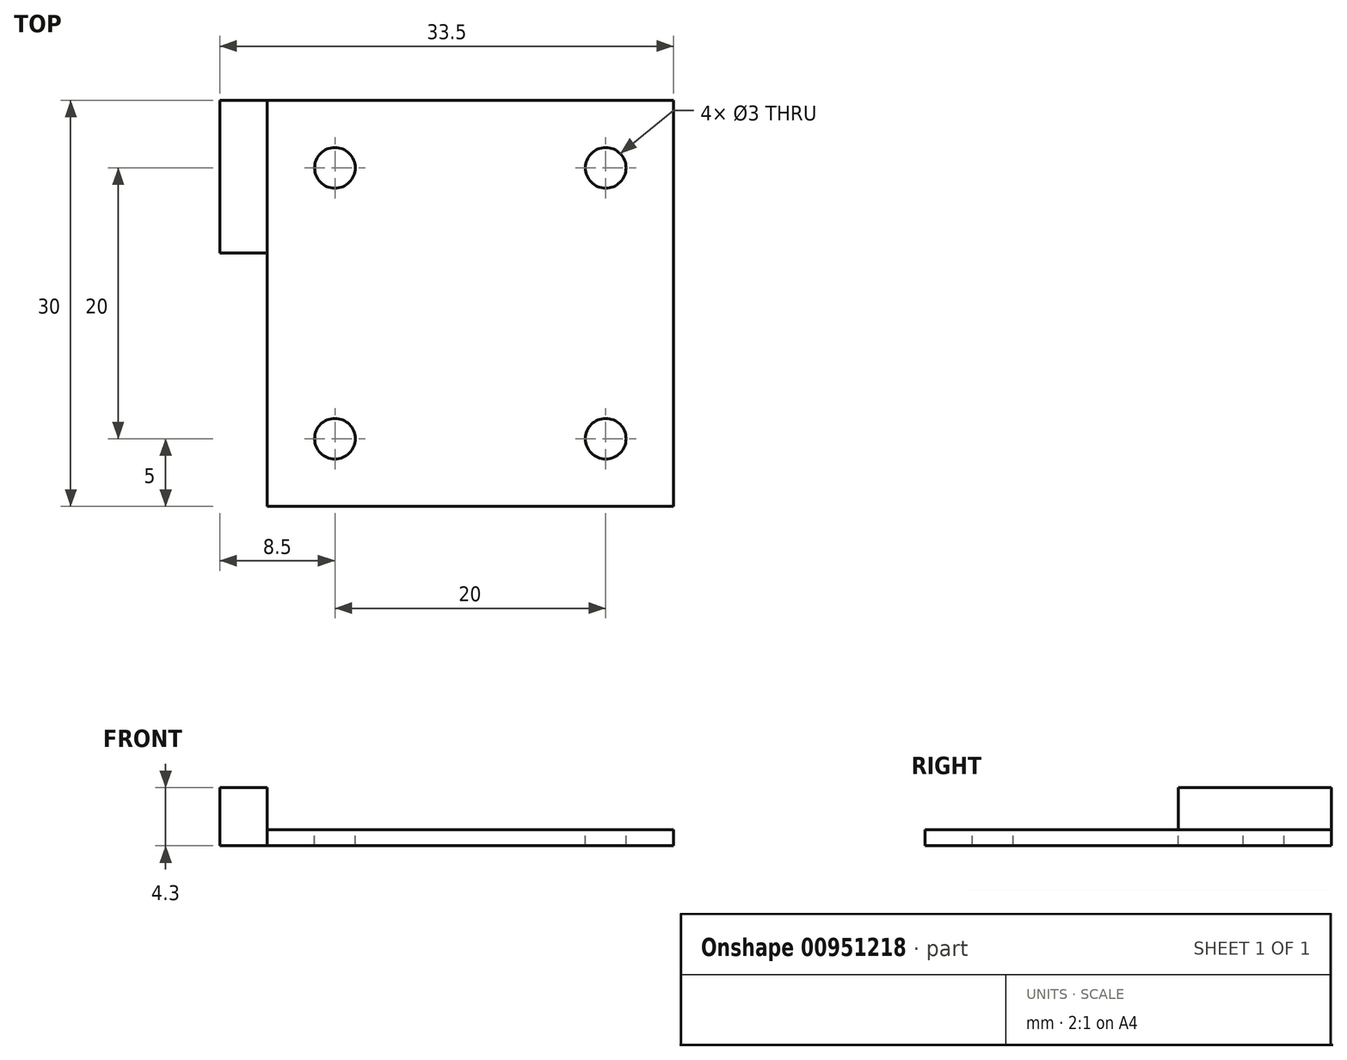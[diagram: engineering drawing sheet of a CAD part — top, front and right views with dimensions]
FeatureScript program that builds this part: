
annotation { "Feature Type Name" : "Feature", "Feature Type Description" : "" }
export const myFeature = defineFeature(function(context is Context, id is Id, definition is map)
    precondition{}
    {
        {
            var Q0;
            Q0=qCreatedBy(makeId("Top.planeOp"),FACE);
            var sketch = newSketch(context, id + "F0", { "sketchPlane" : qUnion([Q0])});
            skLineSegment(sketch, "E0.bottom", {"start": v(-15, 15) * mm, "end": v(15, 15) * mm});
            skLineSegment(sketch, "E0.top", {"start": v(-15, -15) * mm, "end": v(15, -15) * mm});
            skLineSegment(sketch, "E0.left", {"start": v(-15, 15) * mm, "end": v(-15, -15) * mm});
            skLineSegment(sketch, "E0.right", {"start": v(15, 15) * mm, "end": v(15, -15) * mm});
            skPoint(sketch, "E0.middle", {"position": v(0, 0) * mm});
            skLineSegment(sketch, "E1.bottom", {"start": v(-15, 15) * mm, "end": v(-18.5, 15) * mm});
            skLineSegment(sketch, "E1.top", {"start": v(-15, 3.7) * mm, "end": v(-18.5, 3.7) * mm});
            skLineSegment(sketch, "E1.left", {"start": v(-15, 15) * mm, "end": v(-15, 3.7) * mm});
            skLineSegment(sketch, "E1.right", {"start": v(-18.5, 15) * mm, "end": v(-18.5, 3.7) * mm});
            skCircle(sketch, "E2", {"center": v(10, 10) * mm, "radius": 1.5 * mm});
            skCircle(sketch, "E3", {"center": v(10, -10) * mm, "radius": 1.5 * mm});
            skCircle(sketch, "E4", {"center": v(-10, 10) * mm, "radius": 1.5 * mm});
            skCircle(sketch, "E5", {"center": v(-10, -10) * mm, "radius": 1.5 * mm});
            skSolve(sketch);
        }
        {
            var Q0;
            Q0=makeQuery(id+"F0.imprint","IMPRINT",FACE,{"disambiguationData":[TD([[makeQuery(id+"F0.imprint","IMPRINT",EDGE,{"derivedFrom":sQuery(id+"F0.wireOp",EDGE,"E1.bottom")}),1.0]])]});
            var Q1;
            Q1=makeQuery(id+"F0.imprint","IMPRINT",FACE,{"disambiguationData":[TD([[makeQuery(id+"F0.imprint","IMPRINT",EDGE,{"derivedFrom":sQuery(id+"F0.wireOp",EDGE,"E0.bottom")}),-1.0]])]});
            extrude(context, id + "F1", {"entities" : qUnion([Q0, Q1]), "oppositeDirection" : true, "depth" : 1.2 * mm, "offsetDistance" : 25 * mm});
        }
        {
            var Q0;
            Q0=makeQuery(id+"F0.imprint","IMPRINT",FACE,{"disambiguationData":[TD([[makeQuery(id+"F0.imprint","IMPRINT",EDGE,{"derivedFrom":sQuery(id+"F0.wireOp",EDGE,"E1.bottom")}),1.0]])]});
            extrude(context, id + "F2", {"entities" : qUnion([Q0]), "operationType" : NewBodyOperationType.ADD, "depth" : 3.1 * mm, "offsetDistance" : 25 * mm});
        }
    });
